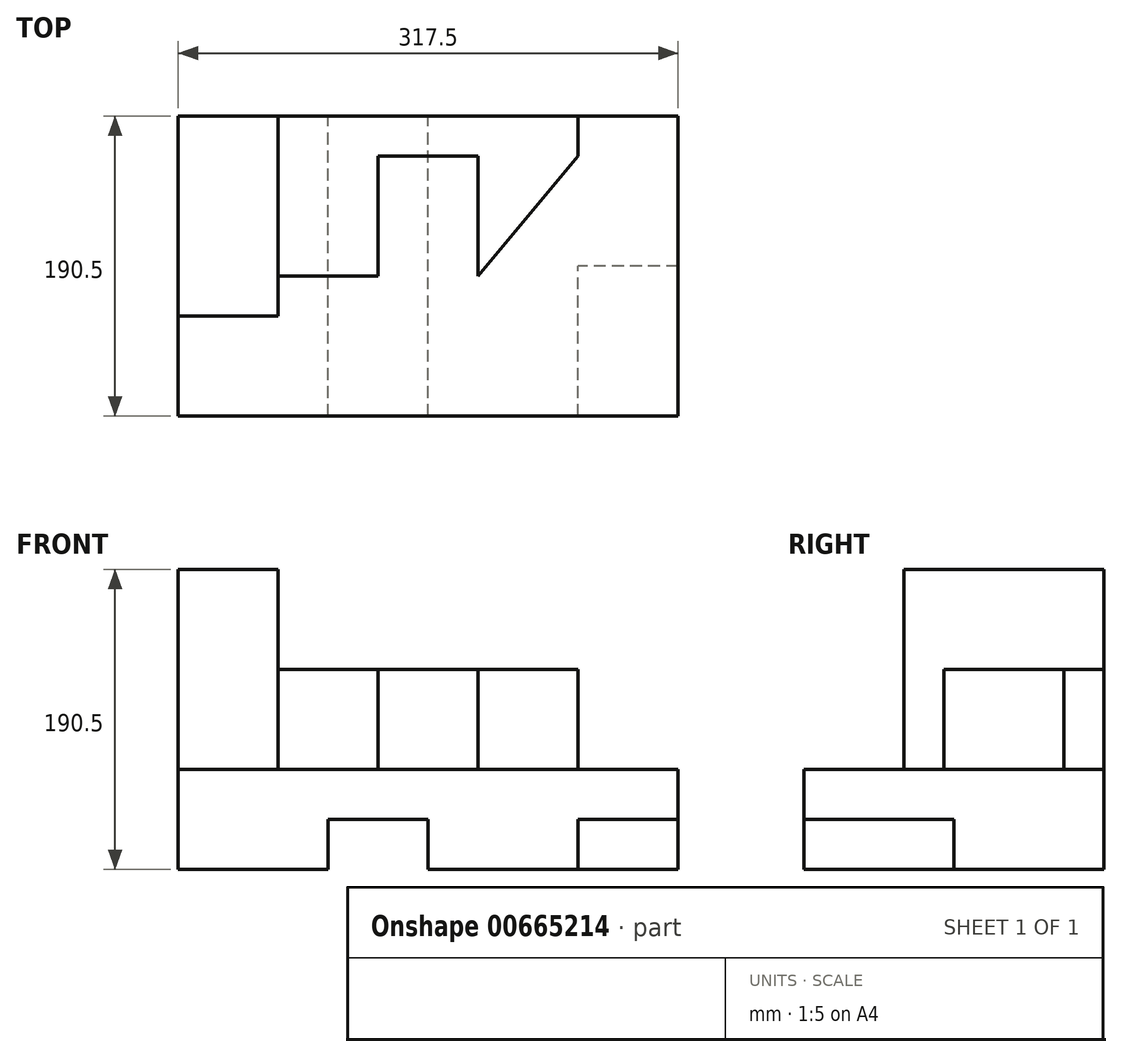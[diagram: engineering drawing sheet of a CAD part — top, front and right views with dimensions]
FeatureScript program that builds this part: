
annotation { "Feature Type Name" : "Feature", "Feature Type Description" : "" }
export const myFeature = defineFeature(function(context is Context, id is Id, definition is map)
    precondition{}
    {
        {
            var Q0;
            Q0=qCreatedBy(makeId("Front.planeOp"),FACE);
            var sketch = newSketch(context, id + "F0", { "sketchPlane" : qUnion([Q0])});
            skLineSegment(sketch, "E0", {"start": v(0, 0) * mm, "end": v(0, 190.5) * mm});
            skLineSegment(sketch, "E1", {"start": v(0, 190.5) * mm, "end": v(63.5, 190.5) * mm});
            skLineSegment(sketch, "E2", {"start": v(63.5, 190.5) * mm, "end": v(63.5, 127) * mm});
            skLineSegment(sketch, "E3", {"start": v(63.5, 127) * mm, "end": v(254, 127) * mm});
            skLineSegment(sketch, "E4", {"start": v(158.75, 0) * mm, "end": v(158.75, 0) * mm});
            skLineSegment(sketch, "E5", {"start": v(158.75, 0) * mm, "end": v(158.75, 31.75) * mm});
            skLineSegment(sketch, "E6", {"start": v(158.75, 31.75) * mm, "end": v(95.25, 31.75) * mm});
            skLineSegment(sketch, "E7", {"start": v(95.25, 31.75) * mm, "end": v(95.25, 0) * mm});
            skLineSegment(sketch, "E8", {"start": v(95.25, 0) * mm, "end": v(0, 0) * mm});
            skLineSegment(sketch, "E9", {"start": v(254, 127) * mm, "end": v(254, 63.5) * mm});
            skLineSegment(sketch, "E10", {"start": v(254, 63.5) * mm, "end": v(317.5, 63.5) * mm});
            skLineSegment(sketch, "E11", {"start": v(317.5, 63.5) * mm, "end": v(317.5, 0) * mm});
            skLineSegment(sketch, "E12", {"start": v(317.5, 0) * mm, "end": v(158.75, 0) * mm});
            skLineSegment(sketch, "E13", {"start": v(254, 63.5) * mm, "end": v(0, 63.5) * mm});
            skLineSegment(sketch, "E14", {"start": v(63.5, 127) * mm, "end": v(63.5, 63.5) * mm});
            skLineSegment(sketch, "E15", {"start": v(127, 127) * mm, "end": v(127, 63.5) * mm});
            skLineSegment(sketch, "E16", {"start": v(190.5, 127) * mm, "end": v(190.5, 63.5) * mm});
            skLineSegment(sketch, "E17", {"start": v(317.5, 31.75) * mm, "end": v(254, 31.75) * mm});
            skLineSegment(sketch, "E18", {"start": v(254, 31.75) * mm, "end": v(254, 0) * mm});
            skSolve(sketch);
        }
        {
            var Q0;
            {var subQ4=sQuery(id+"F0.wireOp",EDGE,"E5");Q0=makeQuery(id+"F0.imprint","IMPRINT",FACE,{"disambiguationData":[TD([[makeQuery(id+"F0.imprint","IMPRINT",EDGE,{"derivedFrom":subQ4}),-1.0]])]});}
            extrude(context, id + "F1", {"entities" : qUnion([Q0]), "depth" : 190.5 * mm, "offsetDistance" : 25.4 * mm});
        }
        {
            var Q0;
            {var subQ4=sQuery(id+"F0.wireOp",EDGE,"E1");Q0=makeQuery(id+"F0.imprint","IMPRINT",FACE,{"disambiguationData":[TD([[makeQuery(id+"F0.imprint","IMPRINT",EDGE,{"derivedFrom":subQ4}),-1.0]])]});}
            extrude(context, id + "F2", {"entities" : qUnion([Q0]), "operationType" : NewBodyOperationType.ADD, "depth" : 127 * mm, "offsetDistance" : 25.4 * mm});
        }
        {
            var Q0;
            {var subQ0=sQuery(id+"F0.wireOp",EDGE,"E14");Q0=makeQuery(id+"F0.imprint","IMPRINT",FACE,{"disambiguationData":[TD([[makeQuery(id+"F0.imprint","IMPRINT",EDGE,{"derivedFrom":subQ0}),1.0]])]});}
            var Q1;
            {var subQ0=sQuery(id+"F0.wireOp",EDGE,"E9");Q1=makeQuery(id+"F0.imprint","IMPRINT",FACE,{"disambiguationData":[TD([[makeQuery(id+"F0.imprint","IMPRINT",EDGE,{"derivedFrom":subQ0}),-1.0]])]});}
            extrude(context, id + "F3", {"entities" : qUnion([Q0, Q1]), "operationType" : NewBodyOperationType.ADD, "depth" : 101.6 * mm, "offsetDistance" : 25.4 * mm});
        }
        {
            var Q0;
            {var subQ0=sQuery(id+"F0.wireOp",EDGE,"E15");Q0=makeQuery(id+"F0.imprint","IMPRINT",FACE,{"disambiguationData":[TD([[makeQuery(id+"F0.imprint","IMPRINT",EDGE,{"derivedFrom":subQ0}),1.0]])]});}
            extrude(context, id + "F4", {"entities" : qUnion([Q0]), "operationType" : NewBodyOperationType.ADD, "depth" : 25.4 * mm, "offsetDistance" : 25.4 * mm});
        }
        {
            var Q0;
            {var subQ3=sQuery(id+"F0.wireOp",EDGE,"E17");Q0=makeQuery(id+"F0.imprint","IMPRINT",FACE,{"disambiguationData":[TD([[makeQuery(id+"F0.imprint","IMPRINT",EDGE,{"derivedFrom":subQ3}),1.0]])]});}
            extrude(context, id + "F5", {"entities" : qUnion([Q0]), "operationType" : NewBodyOperationType.ADD, "depth" : 95.25 * mm, "offsetDistance" : 25.4 * mm});
        }
        {
            var Q0;
            {var subQ0=sQuery(id+"F0.wireOp",EDGE,"E3");Q0=makeQuery(id+"F4.boolean.opBoolean","MERGE",FACE,{"derivedFrom":[makeQuery(id+"F3.opExtrude","SWEPT_FACE",FACE,{"disambiguationData":[OSD([subQ0]),TDD([makeQuery(id+"F0.imprint","IMPRINT",EDGE,{"disambiguationData":[TD([[makeQuery(id+"F0.imprint","INTERSECT",VERTEX,{"derivedFrom":[subQ0,sQuery(id+"F0.wireOp",EDGE,"E15")]}),1.0]])],"derivedFrom":subQ0})])]}),makeQuery(id+"F3.opExtrude","SWEPT_FACE",FACE,{"disambiguationData":[OSD([subQ0]),TDD([makeQuery(id+"F0.imprint","IMPRINT",EDGE,{"disambiguationData":[TD([[makeQuery(id+"F0.imprint","INTERSECT",VERTEX,{"derivedFrom":[subQ0,sQuery(id+"F0.wireOp",EDGE,"E9")]}),1.0]])],"derivedFrom":subQ0})])]}),makeQuery(id+"F4.opExtrude","SWEPT_FACE",FACE,{"disambiguationData":[OSD([subQ0])]})]});}
            var sketch = newSketch(context, id + "F6", { "sketchPlane" : qUnion([Q0])});
            skLineSegment(sketch, "E19", {"start": v(190.5, -101.6) * mm, "end": v(254, -25.4) * mm});
            skLineSegment(sketch, "E20", {"start": v(254, -25.4) * mm, "end": v(254, -101.6) * mm});
            skLineSegment(sketch, "E21", {"start": v(254, -101.6) * mm, "end": v(190.5, -101.6) * mm});
            skSolve(sketch);
        }
        {
            var Q0;
            Q0=makeQuery(id+"F6.imprint","IMPRINT",FACE,{"disambiguationData":[TD([[makeQuery(id+"F6.imprint","IMPRINT",EDGE,{"derivedFrom":sQuery(id+"F6.wireOp",EDGE,"E19")}),-1.0]])]});
            extrude(context, id + "F7", {"entities" : qUnion([Q0]), "operationType" : NewBodyOperationType.REMOVE, "oppositeDirection" : true, "depth" : 63.5 * mm, "offsetDistance" : 25.4 * mm});
        }
    });
